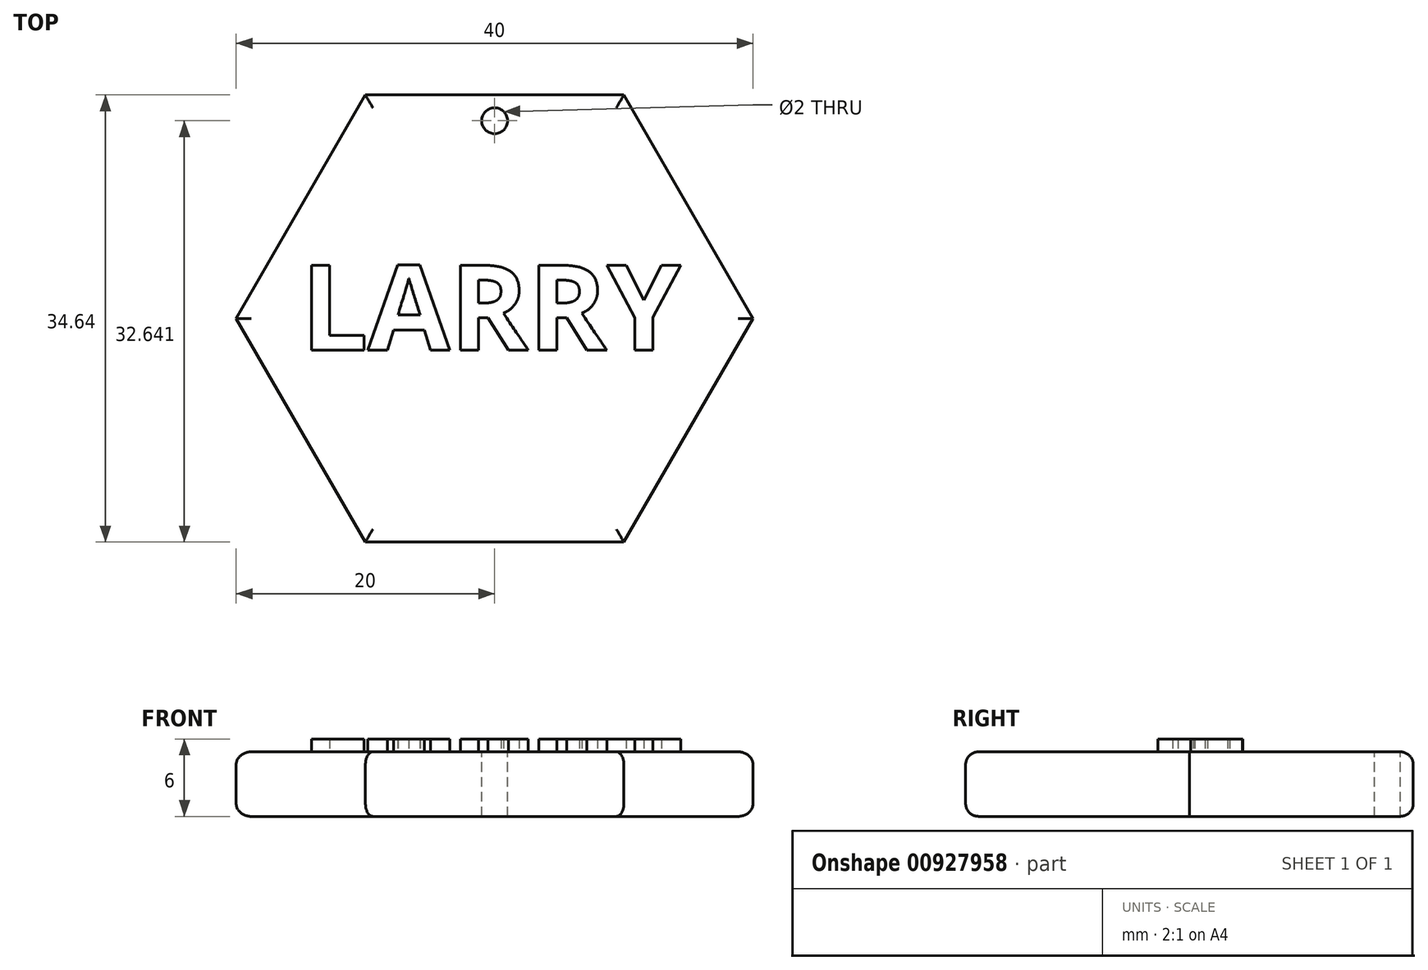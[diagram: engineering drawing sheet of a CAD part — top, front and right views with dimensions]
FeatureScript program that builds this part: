
annotation { "Feature Type Name" : "Feature", "Feature Type Description" : "" }
export const myFeature = defineFeature(function(context is Context, id is Id, definition is map)
    precondition{}
    {
        {
            var Q0;
            Q0=qCreatedBy(makeId("Top.planeOp"),FACE);
            var sketch = newSketch(context, id + "F0", { "sketchPlane" : qUnion([Q0])});
            skLineSegment(sketch, "E0", {"start": v(-10, 17.32) * mm, "end": v(10, 17.32) * mm});
            skLineSegment(sketch, "E1", {"start": v(10, 17.32) * mm, "end": v(20, 0) * mm});
            skLineSegment(sketch, "E2", {"start": v(20, 0) * mm, "end": v(10, -17.32) * mm});
            skLineSegment(sketch, "E3", {"start": v(10, -17.32) * mm, "end": v(-10, -17.32) * mm});
            skLineSegment(sketch, "E4", {"start": v(-10, -17.32) * mm, "end": v(-20, 0) * mm});
            skLineSegment(sketch, "E5", {"start": v(-20, 0) * mm, "end": v(-10, 17.32) * mm});
            skPoint(sketch, "E6.orphan", {"position": v(40, 0) * mm});
            skPoint(sketch, "E7.orphan", {"position": v(-40, 0) * mm});
            skPoint(sketch, "E8.start.orphan", {"position": v(0, 0) * mm});
            skSolve(sketch);
        }
        {
            var Q0;
            Q0 = qSketchRegion(id + "F0", true);
            extrude(context, id + "F1", {"entities" : qUnion([Q0]), "depth" : 5 * mm, "offsetDistance" : 25 * mm});
        }
        {
            var Q0;
            Q0=makeQuery(id+"F1.opExtrude","CAP_FACE",FACE,{"disambiguationData":[OSD([sQuery(id+"F0.wireOp",EDGE,"E0"),sQuery(id+"F0.wireOp",EDGE,"E1"),sQuery(id+"F0.wireOp",EDGE,"E2"),sQuery(id+"F0.wireOp",EDGE,"E3"),sQuery(id+"F0.wireOp",EDGE,"E4"),sQuery(id+"F0.wireOp",EDGE,"E5")])],"isStart":false});
            var sketch = newSketch(context, id + "F2", { "sketchPlane" : qUnion([Q0])});
            skCircle(sketch, "E9", {"center": v(0, 15.32) * mm, "radius": 1 * mm});
            skSolve(sketch);
        }
        {
            var Q0;
            Q0 = qSketchRegion(id + "F2", true);
            extrude(context, id + "F3", {"entities" : qUnion([Q0]), "operationType" : NewBodyOperationType.REMOVE, "oppositeDirection" : true, "depth" : 25 * mm, "offsetDistance" : 25 * mm});
        }
        {
            var Q0;
            Q0=makeQuery(id+"F1.opExtrude","CAP_FACE",FACE,{"disambiguationData":[OSD([sQuery(id+"F0.wireOp",EDGE,"E0"),sQuery(id+"F0.wireOp",EDGE,"E1"),sQuery(id+"F0.wireOp",EDGE,"E2"),sQuery(id+"F0.wireOp",EDGE,"E3"),sQuery(id+"F0.wireOp",EDGE,"E4"),sQuery(id+"F0.wireOp",EDGE,"E5")])],"isStart":false});
            var sketch = newSketch(context, id + "F4", { "sketchPlane" : qUnion([Q0])});
            skText(sketch, "E10", { "text": "LARRY", "fontName": "OpenSans-Bold.ttf"});
            const initialGuessF4  = {"E10": [-0.015, -0.00245, 1, 0, 0.00662]};
            skSetInitialGuess(sketch, initialGuessF4);
            skSolve(sketch);
        }
        {
            var Q0;
            Q0 = qSketchRegion(id + "F4", true);
            extrude(context, id + "F5", {"entities" : qUnion([Q0]), "operationType" : NewBodyOperationType.ADD, "depth" : 1 * mm, "offsetDistance" : 25 * mm});
        }
        {
            var Q0;
            Q0=makeQuery(id+"F1.opExtrude","CAP_EDGE",EDGE,{"disambiguationData":[OSD([sQuery(id+"F0.wireOp",EDGE,"E2")])],"isStart":false});
            var Q1;
            Q1=makeQuery(id+"F1.opExtrude","CAP_EDGE",EDGE,{"disambiguationData":[OSD([sQuery(id+"F0.wireOp",EDGE,"E4")])],"isStart":false});
            var Q2;
            Q2=makeQuery(id+"F1.opExtrude","CAP_EDGE",EDGE,{"disambiguationData":[OSD([sQuery(id+"F0.wireOp",EDGE,"E3")])],"isStart":false});
            var Q3;
            Q3=makeQuery(id+"F1.opExtrude","CAP_EDGE",EDGE,{"disambiguationData":[OSD([sQuery(id+"F0.wireOp",EDGE,"E1")])],"isStart":false});
            var Q4;
            Q4=makeQuery(id+"F1.opExtrude","CAP_EDGE",EDGE,{"disambiguationData":[OSD([sQuery(id+"F0.wireOp",EDGE,"E0")])],"isStart":false});
            var Q5;
            Q5=makeQuery(id+"F1.opExtrude","CAP_EDGE",EDGE,{"disambiguationData":[OSD([sQuery(id+"F0.wireOp",EDGE,"E5")])],"isStart":false});
            var Q6;
            Q6=makeQuery(id+"F1.opExtrude","CAP_EDGE",EDGE,{"disambiguationData":[OSD([sQuery(id+"F0.wireOp",EDGE,"E1")])],"isStart":true});
            var Q7;
            Q7=makeQuery(id+"F1.opExtrude","CAP_EDGE",EDGE,{"disambiguationData":[OSD([sQuery(id+"F0.wireOp",EDGE,"E2")])],"isStart":true});
            var Q8;
            Q8=makeQuery(id+"F1.opExtrude","CAP_EDGE",EDGE,{"disambiguationData":[OSD([sQuery(id+"F0.wireOp",EDGE,"E3")])],"isStart":true});
            var Q9;
            Q9=makeQuery(id+"F1.opExtrude","CAP_EDGE",EDGE,{"disambiguationData":[OSD([sQuery(id+"F0.wireOp",EDGE,"E4")])],"isStart":true});
            var Q10;
            Q10=makeQuery(id+"F1.opExtrude","CAP_EDGE",EDGE,{"disambiguationData":[OSD([sQuery(id+"F0.wireOp",EDGE,"E5")])],"isStart":true});
            var Q11;
            Q11=makeQuery(id+"F1.opExtrude","CAP_EDGE",EDGE,{"disambiguationData":[OSD([sQuery(id+"F0.wireOp",EDGE,"E0")])],"isStart":true});
            fillet(context, id + "F6", {"entities" : qUnion([Q0, Q1, Q2, Q3, Q4, Q5, Q6, Q7, Q8, Q9, Q10, Q11]), "radius" : 1 * mm, "tangentPropagation" : true, "allowEdgeOverflow" : false});
        }
    });
